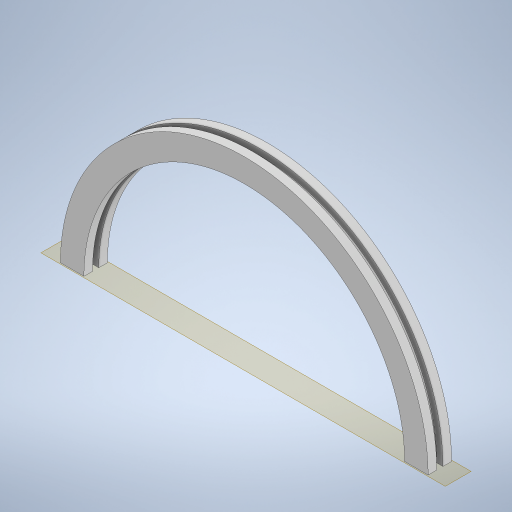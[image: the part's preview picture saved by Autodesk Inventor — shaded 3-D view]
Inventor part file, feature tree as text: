
AUTODESK INVENTOR PART (.ipt)
format: ipt  version: 2023 (Build 270158000, 158)  size: 268,288 bytes
history: native  units: mm
features: sketch x2, sweep x1
ambient origin geometry x8: Origin, YZ Plane, XZ Plane, XY Plane, X Axis, Y Axis, Z Axis, Center Point
bodies: Solid1 (feature_tree)
feature tree (3):
  sweep  "Sweep1"
  sketch  "Sketch1"  dims[d1=440.0mm d5=100.0mm]
  sketch  "Sketch2"  dims[d17=220.0mm d18=8.0mm d19=8.0mm d21=14.0mm d22=30.0mm d23=15.0mm d24=4.0mm d25=7.0mm d26=0.0mm d27=0.0mm]
